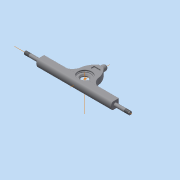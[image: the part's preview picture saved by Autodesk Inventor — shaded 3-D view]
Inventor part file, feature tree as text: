
AUTODESK INVENTOR PART (.ipt)
format: ipt  version: 2014 (Build 180170000, 170)  size: 356,352 bytes
history: native  units: in
note: dims shown in document units (in); Inventor stores cm internally (conversion verified against a paired STEP export)
features: extrude x10, sketch x7, fillet x5, other x4, thread x2, projected_geometry x2, plane x1, mirror x1, chamfer x1
ambient origin geometry x8: Origin, YZ Plane, XZ Plane, XY Plane, X Axis, Y Axis, Z Axis, Center Point
bodies: Solid1 (feature_tree)
feature tree (33):
  sketch  "Sketch1"  dims[d0=0.71in d1=0.74in]
  extrude  "Extrusion1"  Depth=0.74in
  extrude  "Extrusion2"  Depth=7.0866in TaperAngle=0.0deg
  extrude  "Extrusion3"  Depth=0.3435in
  extrude  "Extrusion4"  Depth=2.7in
  fillet  "Fillet1"  Radius=2.7in
  fillet  "Fillet2"  Radius=1.85in
  extrude  "Extrusion5"  Depth=0.06in
  fillet  "Fillet3"  Radius=0.5in
  fillet  "Fillet4"  Radius=0.5in
  sketch  "Sketch5"  dims[d15=0.06in d17=0.06in d18=0.5in d19=0.5in d20=0.0in]
  plane  "Work Plane1"
  extrude  "Extrusion6"  Depth=0.9055in
  extrude  "Extrusion7"  Depth=0.02in
  extrude  "Extrusion8"  Depth=0.02in
  mirror  "Mirror1"
  extrude  "Extrusion9"  Depth=0.02in
  extrude  "Extrusion10"  Depth=0.3175in
  thread  "Thread1"  [1 undecoded]
  thread  "Thread2"  [1 undecoded]
  fillet  "Fillet5"  Radius=0.225in
  other  "Work Axis1"
  other  "Work Axis2"
  other  "Work Point1"
  chamfer  "Chamfer1"  Distance=0.17in
  sketch  "Sketch2"  dims[d2=0.535in d3=7.0866in d4=0.0in]
  sketch  "Sketch3"  dims[d5=0.3125in d6=0.3435in]
  projected_geometry  "Projected Loop1"
  sketch  "Sketch4"  dims[d7=3.543in d8=0.0in d9=9.9213in d10=0.0in d11=2.7in d12=2.7in d13=1.85in d14=0.0in]
  projected_geometry  "Projected Loop2"
  sketch  "Sketch6"  dims[d21=0.25in d22=0.9055in]
  sketch  "Sketch7"  dims[d23=0.0in d24=0.0in d25=1.9685in d26=0.7874in d27=0.635in d28=0.3175in d30=0.33in d31=0.0in d32=0.0in d33=0.225in d34=0.0in d35=0.17in d36=0.0in d37=1.2in d38=0.655in d39=0.345in d40=0.32in d41=0.05in d42=0.1in d43=0.0in d44=0.622in d45=0.58in d46=0.481in d47=0.35in d48=0.3in d49=0.025in d50=0.0in d51=0.45in d52=0.0in d53=0.45in d54=0.0in d55=0.02in d56=0.1in d57=0.125in d58=45.0deg]
  other  "Work Axis3"
note: 2 required parameter values undecoded (feature->parameter linkage not recoverable at this tier; creation-order binding heuristic only, values carry confidence <= 0.55)
